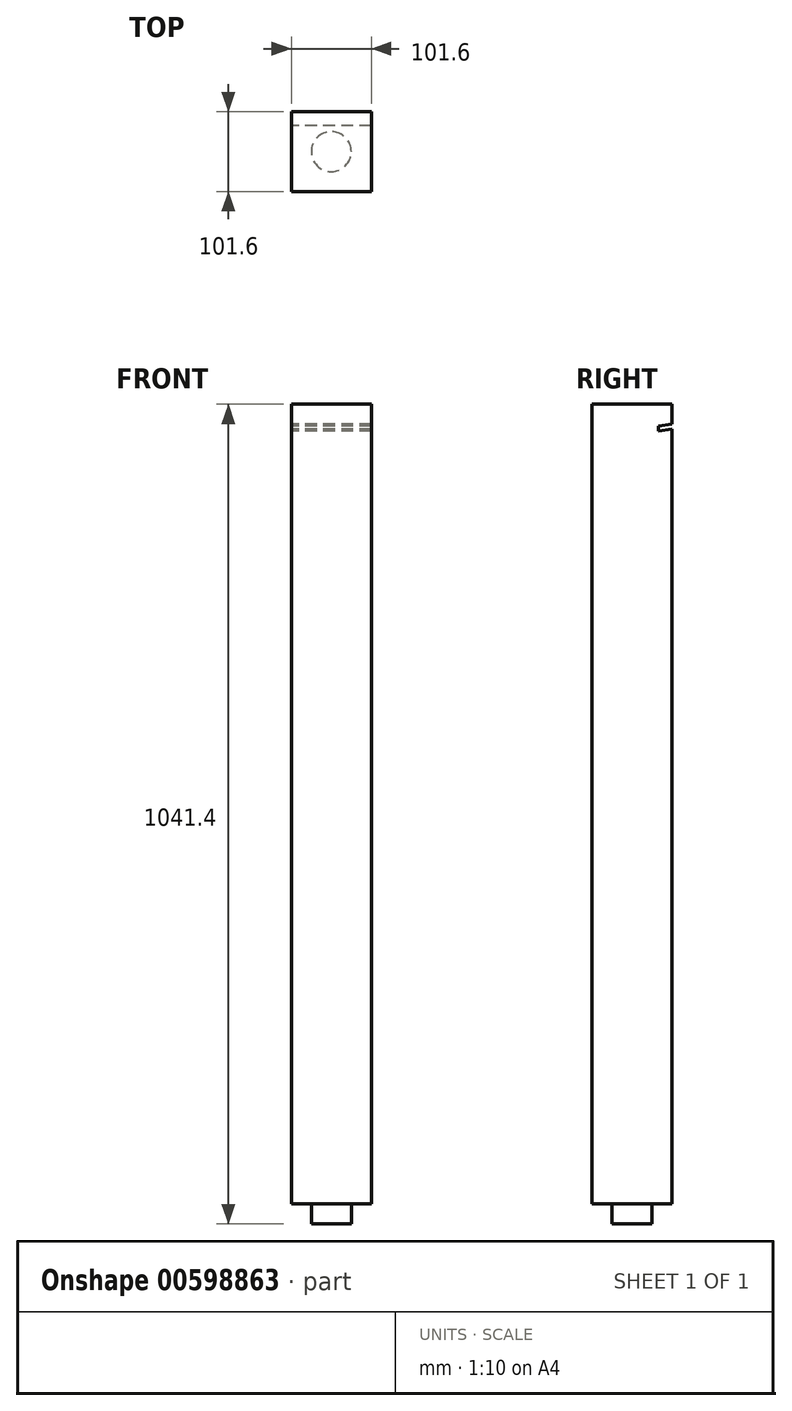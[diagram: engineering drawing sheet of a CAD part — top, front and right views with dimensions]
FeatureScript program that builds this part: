
annotation { "Feature Type Name" : "Feature", "Feature Type Description" : "" }
export const myFeature = defineFeature(function(context is Context, id is Id, definition is map)
    precondition{}
    {
        {
            var Q0;
            Q0=qCreatedBy(makeId("Top.planeOp"),FACE);
            var sketch = newSketch(context, id + "F0", { "sketchPlane" : qUnion([Q0])});
            skCircle(sketch, "E0", {"center": v(0, 0) * mm, "radius": 25.4 * mm});
            skSolve(sketch);
        }
        {
            var Q0;
            Q0 = qSketchRegion(id + "F0", true);
            extrude(context, id + "F1", {"entities" : qUnion([Q0]), "depth" : 25.4 * mm, "offsetDistance" : 25.4 * mm});
        }
        {
            var Q0;
            Q0=makeQuery(id+"F1.opExtrude","CAP_FACE",FACE,{"disambiguationData":[OSD([sQuery(id+"F0.wireOp",EDGE,"E0")])],"isStart":false});
            var sketch = newSketch(context, id + "F2", { "sketchPlane" : qUnion([Q0])});
            skLineSegment(sketch, "E1.bottom", {"start": v(-50.8, 50.8) * mm, "end": v(50.8, 50.8) * mm});
            skLineSegment(sketch, "E1.top", {"start": v(-50.8, -50.8) * mm, "end": v(50.8, -50.8) * mm});
            skLineSegment(sketch, "E1.left", {"start": v(-50.8, 50.8) * mm, "end": v(-50.8, -50.8) * mm});
            skLineSegment(sketch, "E1.right", {"start": v(50.8, 50.8) * mm, "end": v(50.8, -50.8) * mm});
            skPoint(sketch, "E1.middle", {"position": v(0, 0) * mm});
            skSolve(sketch);
        }
        {
            var Q0;
            Q0 = qSketchRegion(id + "F2", true);
            extrude(context, id + "F3", {"entities" : qUnion([Q0]), "operationType" : NewBodyOperationType.ADD, "depth" : 1016 * mm, "offsetDistance" : 25.4 * mm});
        }
        {
            var Q0;
            Q0=makeQuery(id+"F3.opExtrude","SWEPT_FACE",FACE,{"disambiguationData":[OSD([sQuery(id+"F2.wireOp",EDGE,"E1.left")])]});
            var sketch = newSketch(context, id + "F4", { "sketchPlane" : qUnion([Q0])});
            skLineSegment(sketch, "E2", {"start": v(-50.8, 1016) * mm, "end": v(-33.15, 1013.82) * mm});
            skLineSegment(sketch, "E3", {"start": v(-33.15, 1013.82) * mm, "end": v(-33.15, 1007.47) * mm});
            skLineSegment(sketch, "E4", {"start": v(-33.15, 1007.47) * mm, "end": v(-50.8, 1009.65) * mm});
            skSolve(sketch);
        }
        {
            var Q0;
            Q0 = qSketchRegion(id + "F4", true);
            var Q1;
            {var subQ0=sQuery(id+"F4.wireOp",EDGE,"E2");Q1=makeQuery(id+"F4.imprint","IMPRINT",FACE,{"disambiguationData":[TD([[makeQuery(id+"F4.imprint","IMPRINT",EDGE,{"derivedFrom":subQ0}),-1.0]])]});}
            extrude(context, id + "F5", {"entities" : qUnion([Q0, Q1]), "operationType" : NewBodyOperationType.REMOVE, "oppositeDirection" : true, "depth" : 101.6 * mm, "offsetDistance" : 25.4 * mm});
        }
    });
